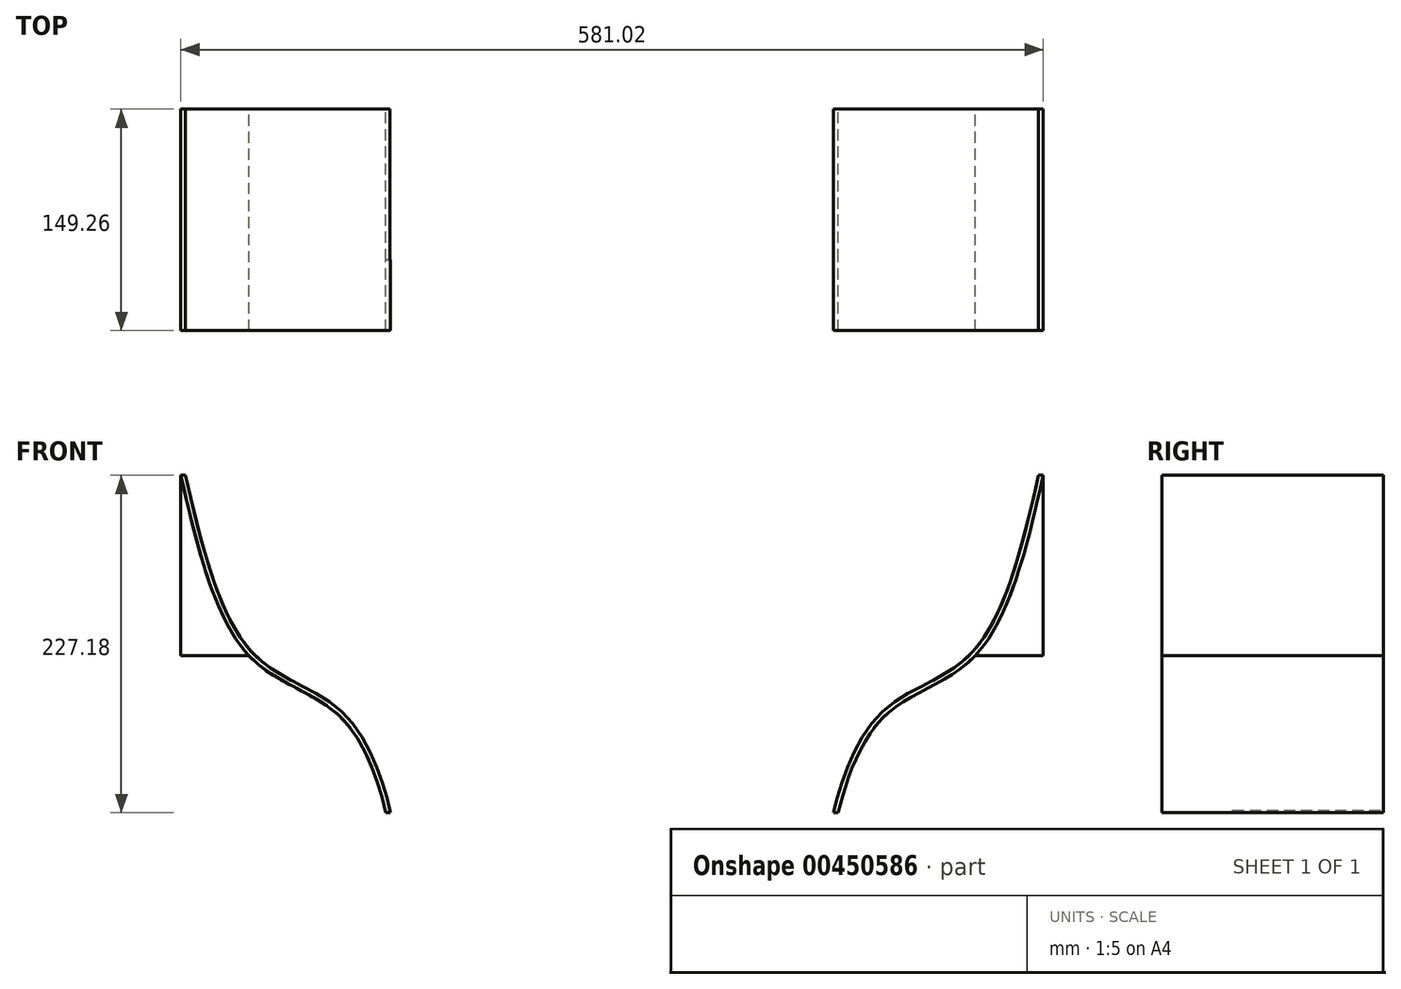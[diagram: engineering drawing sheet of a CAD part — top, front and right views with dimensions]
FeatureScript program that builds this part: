
annotation { "Feature Type Name" : "Feature", "Feature Type Description" : "" }
export const myFeature = defineFeature(function(context is Context, id is Id, definition is map)
    precondition{}
    {
        {
            var Q0;
            Q0=qCreatedBy(makeId("Front.planeOp"),FACE);
            var sketch = newSketch(context, id + "F0", { "sketchPlane" : qUnion([Q0])});
            skLineSegment(sketch, "E0.bottom", {"start": v(290.51, -161.92) * mm, "end": v(-290.51, -161.93) * mm, "construction": true});
            skLineSegment(sketch, "E0.top", {"start": v(290.51, 161.93) * mm, "end": v(-290.51, 161.93) * mm, "construction": true});
            skLineSegment(sketch, "E0.left", {"start": v(290.51, -161.92) * mm, "end": v(290.51, 161.93) * mm, "construction": true});
            skLineSegment(sketch, "E0.right", {"start": v(-290.51, -161.93) * mm, "end": v(-290.51, 161.93) * mm, "construction": true});
            skPoint(sketch, "E0.middle", {"position": v(0, 0) * mm});
            skPoint(sketch, "E1", {"position": v(157.16, -161.93) * mm});
            skPoint(sketch, "E2", {"position": v(-152.4, -161.93) * mm});
            skFitSpline(sketch, "E3", {"points": [v(-290.51, 161.93) * mm, v(-244.59, 40.37) * mm, v(-183.76, 0) * mm, v(-152.4, -65.25) * mm], "startDerivative": vector(77.13, -333.51) * mm, "endDerivative": vector(50.5, -211.24) * mm});
            skLineSegment(sketch, "E4", {"start": v(0, 161.92) * mm, "end": v(0, -161.93) * mm, "construction": true});
            skFitSpline(sketch, "E5.MirrorCS", {"points": [v(290.51, 161.93) * mm, v(244.59, 40.37) * mm, v(183.76, 0) * mm, v(152.4, -65.25) * mm], "startDerivative": vector(-77.13, -333.51) * mm, "endDerivative": vector(-50.5, -211.24) * mm});
            skLineSegment(sketch, "E6", {"start": v(157.16, -161.92) * mm, "end": v(-152.4, -161.93) * mm});
            skLineSegment(sketch, "E7", {"start": v(290.51, 161.93) * mm, "end": v(-290.51, 161.93) * mm});
            skLineSegment(sketch, "E8", {"start": v(-290.51, 161.93) * mm, "end": v(-290.51, 40.37) * mm});
            skLineSegment(sketch, "E9", {"start": v(290.51, 40.37) * mm, "end": v(290.51, 161.93) * mm});
            skLineSegment(sketch, "E10", {"start": v(-290.51, 40.37) * mm, "end": v(-244.59, 40.37) * mm});
            skLineSegment(sketch, "E11", {"start": v(244.59, 40.37) * mm, "end": v(290.51, 40.37) * mm});
            skSolve(sketch);
        }
        {
            var Q0;
            Q0=sQuery(id+"F0.wireOp",VERTEX,"E5.MirrorCS.start");
            var Q1;
            Q1=qCreatedBy(makeId("Top.planeOp"),FACE);
            cPlane(context, id + "F1", {"entities" : qUnion([Q0, Q1]), "cplaneType" : CPlaneType.PLANE_POINT, "offset" : 25.4 * mm, "width" : 152.4 * mm, "height" : 152.4 * mm});
        }
        {
            var Q0;
            Q0=qCreatedBy(id+"F1.planeOp",FACE);
            var sketch = newSketch(context, id + "F2", { "sketchPlane" : qUnion([Q0])});
            skLineSegment(sketch, "E12.bottom", {"start": v(290.51, -74.61) * mm, "end": v(287.34, -74.61) * mm});
            skLineSegment(sketch, "E12.top", {"start": v(290.51, 74.61) * mm, "end": v(287.34, 74.61) * mm});
            skLineSegment(sketch, "E12.left", {"start": v(290.51, -74.61) * mm, "end": v(290.51, 74.61) * mm});
            skLineSegment(sketch, "E12.right", {"start": v(287.34, -74.61) * mm, "end": v(287.34, 74.61) * mm});
            skPoint(sketch, "E12.middle", {"position": v(288.92, 0) * mm});
            skLineSegment(sketch, "E13", {"start": v(0, 74.77) * mm, "end": v(0, -65.56) * mm, "construction": true});
            skLineSegment(sketch, "E14.MirrorCS", {"start": v(-287.34, -74.61) * mm, "end": v(-287.34, 74.61) * mm});
            skLineSegment(sketch, "E15.MirrorCS", {"start": v(-290.51, -74.61) * mm, "end": v(-290.51, 74.61) * mm});
            skLineSegment(sketch, "E16.MirrorCS", {"start": v(-290.51, 74.61) * mm, "end": v(-287.34, 74.61) * mm});
            skLineSegment(sketch, "E17.MirrorCS", {"start": v(-290.51, -74.61) * mm, "end": v(-287.34, -74.61) * mm});
            skSolve(sketch);
        }
        {
            var Q0;
            Q0=makeQuery(id+"F2.imprint","IMPRINT",FACE,{"disambiguationData":[TD([[makeQuery(id+"F2.imprint","IMPRINT",EDGE,{"derivedFrom":sQuery(id+"F2.wireOp",EDGE,"E12.bottom")}),-1.0]])]});
            var Q1;
            Q1=sQuery(id+"F0.wireOp",EDGE,"E5.MirrorCS");
            var Q2;
            Q2=sQuery(id+"F0.wireOp",EDGE,"c529eca6-2d64-4533-bdf1-a865913807980.MirrorCS");
            sweep(context, id + "F3", {"profiles" : qUnion([Q0]), "path" : qUnion([Q1, Q2])});
        }
        {
            var Q0;
            Q0=makeQuery(id+"F3.opSweep","SWEPT_BODY",BODY,{"disambiguationData":[OSD([sQuery(id+"F0.wireOp",EDGE,"E5.MirrorCS"),sQuery(id+"F2.wireOp",EDGE,"E12.bottom"),sQuery(id+"F2.wireOp",EDGE,"E12.top"),sQuery(id+"F2.wireOp",EDGE,"E12.left"),sQuery(id+"F2.wireOp",EDGE,"E12.right")])]});
            var Q1;
            Q1=qCreatedBy(makeId("Right.planeOp"),FACE);
            mirror(context, id + "F4", {"entities" : qUnion([Q0]), "mirrorPlane" : qUnion([Q1])});
        }
        {
            var Q0;
            Q0=makeQuery(id+"F3.opSweep","SWEPT_FACE",FACE,{"disambiguationData":[OSD([sQuery(id+"F0.wireOp",EDGE,"E5.MirrorCS"),sQuery(id+"F2.wireOp",EDGE,"E12.top")])]});
            var sketch = newSketch(context, id + "F5", { "sketchPlane" : qUnion([Q0])});
            skLineSegment(sketch, "E18", {"start": v(-152.4, -65.25) * mm, "end": v(-149.62, -63.56) * mm});
            skLineSegment(sketch, "E19", {"start": v(-149.62, -63.56) * mm, "end": v(-149.23, -65.22) * mm});
            skLineSegment(sketch, "E20", {"start": v(-149.23, -65.22) * mm, "end": v(-152.4, -65.25) * mm});
            skLineSegment(sketch, "E21", {"start": v(0, -138.87) * mm, "end": v(0, -185.76) * mm, "construction": true});
            skLineSegment(sketch, "E22.MirrorCS", {"start": v(152.4, -65.25) * mm, "end": v(149.62, -63.56) * mm});
            skLineSegment(sketch, "E23.MirrorCS", {"start": v(149.62, -63.56) * mm, "end": v(149.23, -65.22) * mm});
            skLineSegment(sketch, "E24.MirrorCS", {"start": v(149.23, -65.22) * mm, "end": v(152.4, -65.25) * mm});
            skSolve(sketch);
        }
        {
            var Q0;
            Q0 = qSketchRegion(id + "F5", true);
            extrude(context, id + "F6", {"entities" : qUnion([Q0]), "operationType" : NewBodyOperationType.REMOVE, "oppositeDirection" : true, "depth" : 101.6 * mm});
        }
        {
            var Q0;
            {var subQ0=sQuery(id+"F0.wireOp",EDGE,"E8");Q0=makeQuery(id+"F0.imprint","IMPRINT",FACE,{"disambiguationData":[TD([[makeQuery(id+"F0.imprint","IMPRINT",EDGE,{"derivedFrom":subQ0}),1.0]])]});}
            var Q1;
            {var subQ0=sQuery(id+"F0.wireOp",EDGE,"E9");Q1=makeQuery(id+"F0.imprint","IMPRINT",FACE,{"disambiguationData":[TD([[makeQuery(id+"F0.imprint","IMPRINT",EDGE,{"derivedFrom":subQ0}),1.0]])]});}
            extrude(context, id + "F7", {"entities" : qUnion([Q0, Q1]), "depth" : 74.63 * mm, "hasSecondDirection" : true, "secondDirectionOppositeDirection" : true, "secondDirectionDepth" : 74.63 * mm});
        }
        {
            var Q0;
            Q0=makeQuery(id+"F6.boolean.opBoolean","COPY",FACE,{"derivedFrom":makeQuery(id+"F6.opExtrude","CAP_FACE",FACE,{"disambiguationData":[OSD([sQuery(id+"F5.wireOp",EDGE,"E18"),sQuery(id+"F5.wireOp",EDGE,"E19"),sQuery(id+"F5.wireOp",EDGE,"E20")])],"isStart":false})});
            var sketch = newSketch(context, id + "F8", { "sketchPlane" : qUnion([Q0])});
            skLineSegment(sketch, "E25", {"start": v(-152.4, -65.25) * mm, "end": v(-149.62, -63.56) * mm});
            skLineSegment(sketch, "E26", {"start": v(-149.62, -63.56) * mm, "end": v(-149.23, -65.22) * mm});
            skLineSegment(sketch, "E27", {"start": v(-149.23, -65.22) * mm, "end": v(-152.4, -65.25) * mm});
            skSolve(sketch);
        }
        {
            var Q0;
            Q0 = qSketchRegion(id + "F8", true);
            extrude(context, id + "F9", {"entities" : qUnion([Q0]), "operationType" : NewBodyOperationType.ADD, "depth" : 101.6 * mm});
        }
    });
